# Revit family: QF_ELECTROLUXPROFESSIONAL_1LSN0M_IS1103_E
name_source: partatom
category: Attrezzature speciali
units: mm (PartAtom-declared; Revit-internal decimal feet)

## family parameters
Basato su piano di lavoro = No
Condiviso = No
Punto di calcolo locali = No
Quota connettore circolare = Usa diametro
Sempre verticale = Sì
Taglio con vuoti quando caricato = No
Tipo di parte = Normale

## types (2) — shared parameters
Cycle = 50 Hz
Depth = 400 mm
Depth Actual = 400 mm
Height = 1050 mm
Height Actual = 1050 mm
Latent Heat Output = 0.0
Length Actual = 1120 mm
Modello = IS1103
Phase = 1
Produttore = Electrolux Professional
Sensible Heat Output = 0.0
URL = www.electroluxprofessional.com
Volts = 230 V
Watts = 3300 W
Weight = 46
Width = 1120 mm
zero-valued in all types: Gas KW, Prospetto di default, Steam Pounds per Hour

## per-type parameters (varying)
| type | Descrizione | Item Number |
| 988703180 | myPRO SMART PROFESSIONAL STEAM IRONER IS1103 1030MM 220-230/50/60/1N 3,3KW SYMBOLS SCHUKO WORKTOP SST | 1LSMZA |
| 988703182 | myPRO SMART PROFESSIONAL STEAM IRONER IS1103 1030MM 230/50/1N 3,3KW SYMBOLS 0 WORKTOP SST | 1LSP6M |

## geometry (parser evidence)
native form markers: Sweep x2
no freeform markers — native parametric forms only
